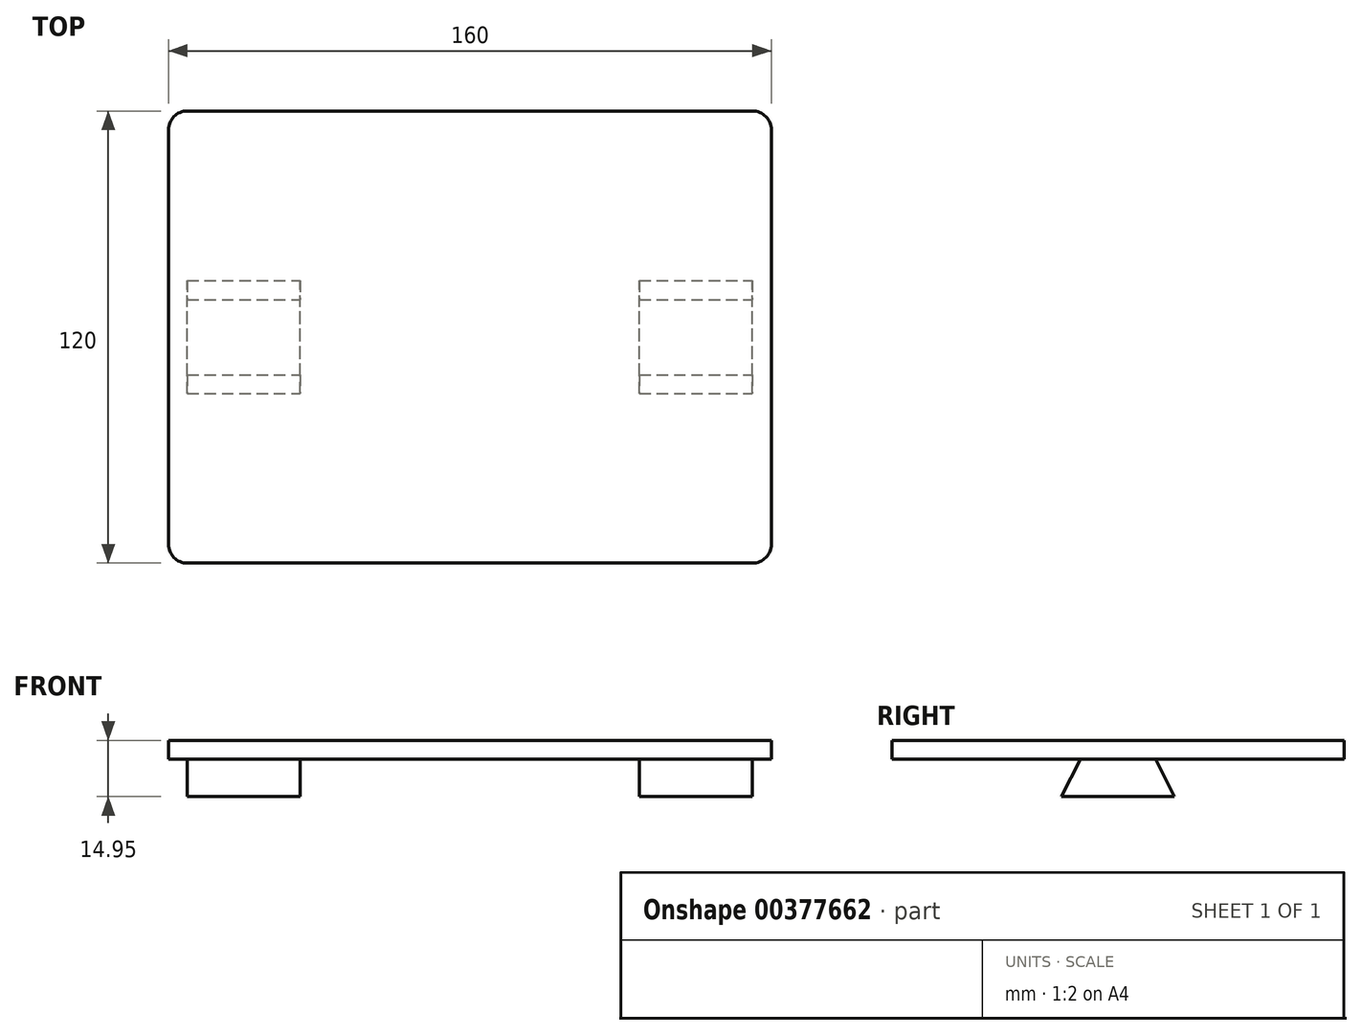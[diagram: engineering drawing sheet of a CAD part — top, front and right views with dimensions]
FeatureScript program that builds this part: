
annotation { "Feature Type Name" : "Feature", "Feature Type Description" : "" }
export const myFeature = defineFeature(function(context is Context, id is Id, definition is map)
    precondition{}
    {
        {
            var Q0;
            Q0=qCreatedBy(makeId("Top.planeOp"),FACE);
            var sketch = newSketch(context, id + "F0", { "sketchPlane" : qUnion([Q0])});
            skLineSegment(sketch, "E0.bottom", {"start": v(-80, 60) * mm, "end": v(80, 60) * mm});
            skLineSegment(sketch, "E0.top", {"start": v(-80, -60) * mm, "end": v(80, -60) * mm});
            skLineSegment(sketch, "E0.left", {"start": v(-80, 60) * mm, "end": v(-80, -60) * mm});
            skLineSegment(sketch, "E0.right", {"start": v(80, 60) * mm, "end": v(80, -60) * mm});
            skPoint(sketch, "E0.middle", {"position": v(0, 0) * mm});
            skSolve(sketch);
        }
        {
            var Q0;
            Q0=makeQuery(id+"F0.imprint","IMPRINT",FACE,{"disambiguationData":[TD([[makeQuery(id+"F0.imprint","IMPRINT",EDGE,{"derivedFrom":sQuery(id+"F0.wireOp",EDGE,"E0.bottom")}),-1.0]])]});
            extrude(context, id + "F1", {"entities" : qUnion([Q0]), "depth" : 5 * mm});
        }
        {
            var Q0;
            Q0=makeQuery(id+"F1.opExtrude","SWEPT_EDGE",EDGE,{"disambiguationData":[OSD([sQuery(id+"F0.wireOp",EDGE,"E0.bottom"),sQuery(id+"F0.wireOp",EDGE,"E0.right")])]});
            var Q1;
            Q1=makeQuery(id+"F1.opExtrude","SWEPT_EDGE",EDGE,{"disambiguationData":[OSD([sQuery(id+"F0.wireOp",EDGE,"E0.top"),sQuery(id+"F0.wireOp",EDGE,"E0.right")])]});
            var Q2;
            Q2=makeQuery(id+"F1.opExtrude","SWEPT_EDGE",EDGE,{"disambiguationData":[OSD([sQuery(id+"F0.wireOp",EDGE,"E0.top"),sQuery(id+"F0.wireOp",EDGE,"E0.left")])]});
            var Q3;
            Q3=makeQuery(id+"F1.opExtrude","SWEPT_EDGE",EDGE,{"disambiguationData":[OSD([sQuery(id+"F0.wireOp",EDGE,"E0.bottom"),sQuery(id+"F0.wireOp",EDGE,"E0.left")])]});
            fillet(context, id + "F2", {"entities" : qUnion([Q0, Q1, Q2, Q3]), "radius" : 5 * mm, "tangentPropagation" : true, "allowEdgeOverflow" : false});
        }
        {
            var Q0;
            Q0=makeQuery(id+"F1.opExtrude","SWEPT_FACE",FACE,{"disambiguationData":[OSD([sQuery(id+"F0.wireOp",EDGE,"E0.right")])]});
            var sketch = newSketch(context, id + "F3", { "sketchPlane" : qUnion([Q0])});
            skLineSegment(sketch, "E1", {"start": v(-9.98, 0) * mm, "end": v(9.97, 0) * mm});
            skLineSegment(sketch, "E2", {"start": v(9.97, 0) * mm, "end": v(14.97, -9.95) * mm});
            skLineSegment(sketch, "E3", {"start": v(14.97, -9.95) * mm, "end": v(-14.98, -9.95) * mm});
            skLineSegment(sketch, "E4", {"start": v(-14.98, -9.95) * mm, "end": v(-9.98, 0) * mm});
            skSolve(sketch);
        }
        {
            var Q0;
            Q0=makeQuery(id+"F3.imprint","IMPRINT",FACE,{"disambiguationData":[TD([[makeQuery(id+"F3.imprint","IMPRINT",EDGE,{"derivedFrom":sQuery(id+"F3.wireOp",EDGE,"E1")}),1.0]])]});
            extrude(context, id + "F4", {"entities" : qUnion([Q0]), "operationType" : NewBodyOperationType.ADD, "oppositeDirection" : true, "depth" : 160 * mm});
        }
        {
            var Q0;
            Q0=qCreatedBy(makeId("Front.planeOp"),FACE);
            var sketch = newSketch(context, id + "F5", { "sketchPlane" : qUnion([Q0])});
            skLineSegment(sketch, "E5.bottom", {"start": v(-45, 0) * mm, "end": v(45, 0) * mm});
            skLineSegment(sketch, "E5.top", {"start": v(-45, -15) * mm, "end": v(45, -15) * mm});
            skLineSegment(sketch, "E5.left", {"start": v(-45, 0) * mm, "end": v(-45, -15) * mm});
            skLineSegment(sketch, "E5.right", {"start": v(45, 0) * mm, "end": v(45, -15) * mm});
            skLineSegment(sketch, "E6.bottom", {"start": v(-80, 0) * mm, "end": v(-75, 0) * mm});
            skLineSegment(sketch, "E6.top", {"start": v(-80, -15) * mm, "end": v(-75, -15) * mm});
            skLineSegment(sketch, "E6.left", {"start": v(-80, 0) * mm, "end": v(-80, -15) * mm});
            skLineSegment(sketch, "E6.right", {"start": v(-75, 0) * mm, "end": v(-75, -15) * mm});
            skLineSegment(sketch, "E7.bottom", {"start": v(80, 0) * mm, "end": v(75, 0) * mm});
            skLineSegment(sketch, "E7.top", {"start": v(80, -15) * mm, "end": v(75, -15) * mm});
            skLineSegment(sketch, "E7.left", {"start": v(80, 0) * mm, "end": v(80, -15) * mm});
            skLineSegment(sketch, "E7.right", {"start": v(75, 0) * mm, "end": v(75, -15) * mm});
            skSolve(sketch);
        }
        {
            var Q0;
            Q0 = qSketchRegion(id + "F5", true);
            extrude(context, id + "F6", {"entities" : qUnion([Q0]), "operationType" : NewBodyOperationType.REMOVE, "depth" : 25 * mm, "hasSecondDirection" : true, "secondDirectionOppositeDirection" : true, "secondDirectionDepth" : 25 * mm});
        }
    });
